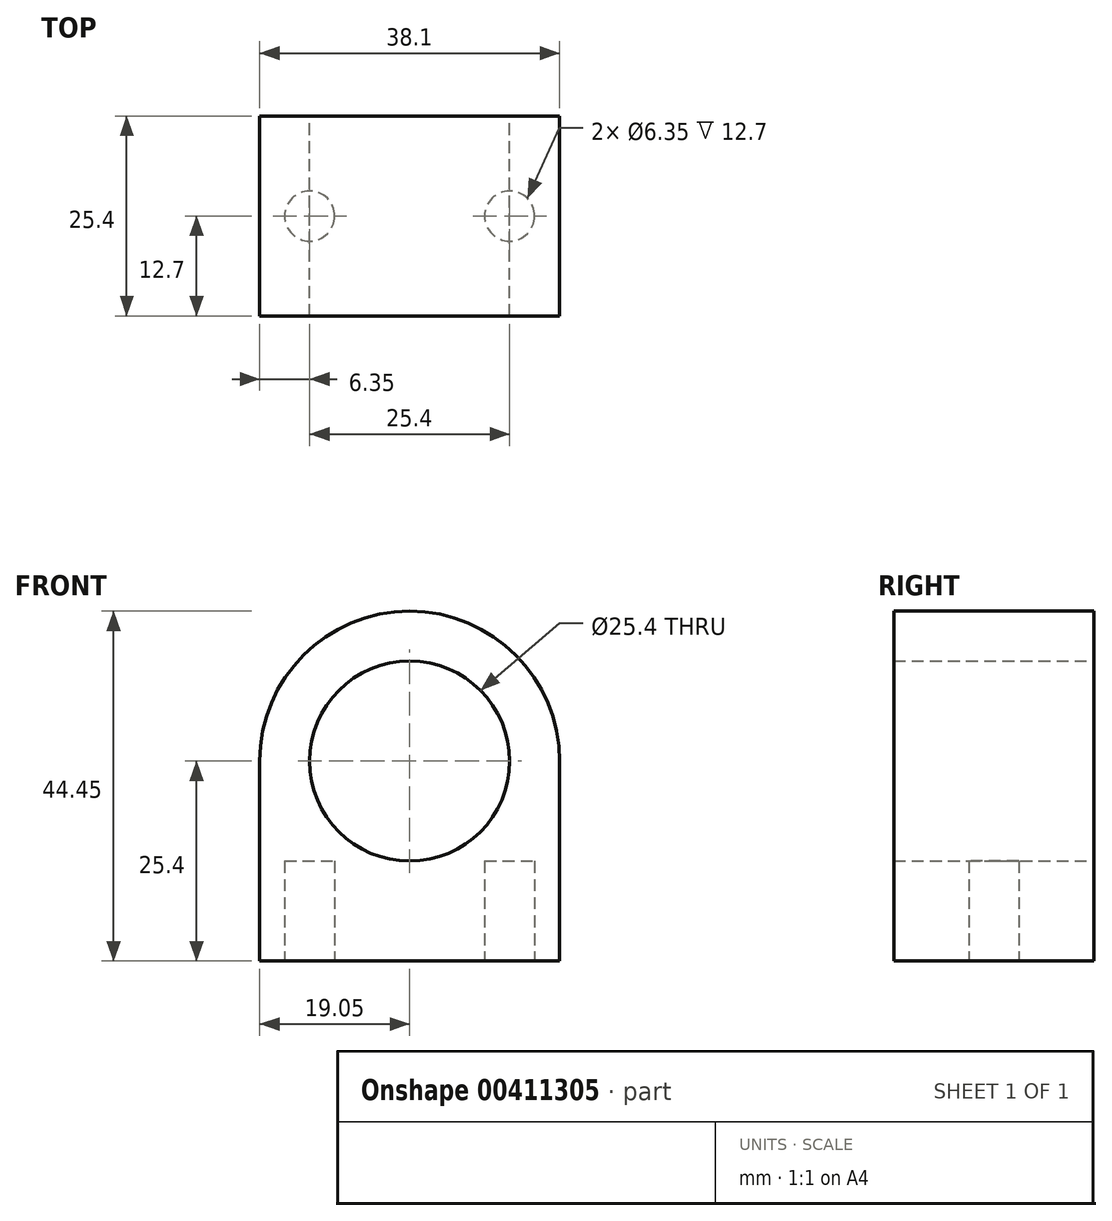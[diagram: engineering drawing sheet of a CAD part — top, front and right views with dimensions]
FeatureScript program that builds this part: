
annotation { "Feature Type Name" : "Feature", "Feature Type Description" : "" }
export const myFeature = defineFeature(function(context is Context, id is Id, definition is map)
    precondition{}
    {
        {
            var Q0;
            Q0=qCreatedBy(makeId("Front.planeOp"),FACE);
            var sketch = newSketch(context, id + "F0", { "sketchPlane" : qUnion([Q0])});
            skArc(sketch, "E0", {"start": v(19.05, 0) * mm, "mid": v(0, 19.05) * mm, "end": v(-19.05, 0) * mm});
            skCircle(sketch, "E1", {"center": v(0, 0) * mm, "radius": 12.7 * mm});
            skLineSegment(sketch, "E2", {"start": v(-19.05, 0) * mm, "end": v(-19.05, -25.4) * mm});
            skLineSegment(sketch, "E3", {"start": v(19.05, 0) * mm, "end": v(19.05, -25.4) * mm});
            skLineSegment(sketch, "E4", {"start": v(19.05, -25.4) * mm, "end": v(-19.05, -25.4) * mm});
            skSolve(sketch);
        }
        {
            var Q0;
            Q0 = qSketchRegion(id + "F0", true);
            extrude(context, id + "F1", {"entities" : qUnion([Q0]), "depth" : 25.4 * mm});
        }
        {
            var Q0;
            Q0=makeQuery(id+"F1.opExtrude","SWEPT_FACE",FACE,{"disambiguationData":[OSD([sQuery(id+"F0.wireOp",EDGE,"E4")])]});
            var sketch = newSketch(context, id + "F2", { "sketchPlane" : qUnion([Q0])});
            skLineSegment(sketch, "E5", {"start": v(-29.38, 12.7) * mm, "end": v(32.23, 12.7) * mm, "construction": true});
            skCircle(sketch, "E6", {"center": v(-12.7, 12.7) * mm, "radius": 3.18 * mm});
            skCircle(sketch, "E7", {"center": v(12.7, 12.7) * mm, "radius": 3.18 * mm});
            skSolve(sketch);
        }
        {
            var Q0;
            Q0 = qSketchRegion(id + "F2", true);
            extrude(context, id + "F3", {"entities" : qUnion([Q0]), "operationType" : NewBodyOperationType.REMOVE, "oppositeDirection" : true, "depth" : 12.7 * mm});
        }
    });
